# Revit family: KEUCO_14920010000
name_source: partatom
category: Allgemeines Modell
revit_build: Autodesk Revit 2016 (Build: 20150220_1215(x64)
units: mm (PartAtom-declared; Revit-internal decimal feet)

## family parameters
Arbeitsebenenbasiert = Ja
Beim Laden mit Abzugskörper schneiden = Nein
Bemaßung runder Anschluss = Durchmesser verwenden
Gemeinsam genutzt = Nein
Immer vertikal = Nein
Kann Basisbauteil für Bewehrung sein = Nein
Raumberechnungspunkt = Nein
Teiletyp = Normal

## types (3) — shared parameters
Hersteller = KEUCO
Rail Length = 450 mm  [stored 1.47638 ft]
Serie = Plan
URL = https://www.keuco.com
Verwendung = GWC / WP
Vorgabe-Ansicht = 1219 mm
zero-valued in all types: Gewicht

## per-type parameters (varying)
| type | Ausschreibungstext | Material |
| 14920010000 | KEUCO PLAN Handtuchhalter, einarmig, 14920010000
Hochglanzverchromter Handtuchhalter, einarmig, 
in ästhetischem, funktionalem Design,
aus rundem Rohr, mit flachem Endstopfen, 
ein feststehender runder Haltearm, antistatisch, 
leicht zu reinigen,
Ausladung 450 mm, Durchmesser 22 mm, 
Rosettendurchmesser 55 mm, Rosettendicke 7 mm, 
der Handtuchhalter wird verdeckt angebracht,
Lieferung inkl. korrosionsfreiem Befestigungsmaterial | Edelstahl |
| 14920070000 | KEUCO PLAN Handtuchhalter, einarmig, 14920070000
Handtuchhalter aus hochwertigem Edelstahl, einarmig, 
in ästhetischem, funktionalem Design,
aus rundem Rohr, mit flachem Endstopfen, 
ein feststehender runder Haltearm, antistatisch, 
leicht zu reinigen,
Ausladung 450 mm, Durchmesser 22 mm, 
Rosettendurchmesser 55 mm, Rosettendicke 7 mm, 
der Handtuchhalter wird verdeckt angebracht,
Lieferung inkl. korrosionsfreiem Befestigungsmaterial | Edelstahl |
| 14920170000 | KEUCO PLAN Handtuchhalter, einarmig, 14920170000
Handtuchhalter aus silber-eloxiertem Aluminium, einarmig, 
in ästhetischem, funktionalem Design,
aus rundem Rohr, mit flachem Endstopfen, 
ein feststehender runder Haltearm, antistatisch, 
leicht zu reinigen,
Ausladung 450 mm, Durchmesser 22 mm, 
Rosettendurchmesser 55 mm, Rosettendicke 7 mm, 
der Handtuchhalter wird verdeckt angebracht,
Lieferung inkl. korrosionsfreiem Befestigungsmaterial | Aluminium silber-eloxiert (E6 EV1) |

note: column(s) folded — value = type name in every type: Artikelnummer

note: [stored X ft] marks values corroborated as IEEE doubles in the binary element streams (Revit-internal decimal feet)

## geometry (parser evidence)
native form markers: Blend x4, Sweep x2
no freeform markers — native parametric forms only
